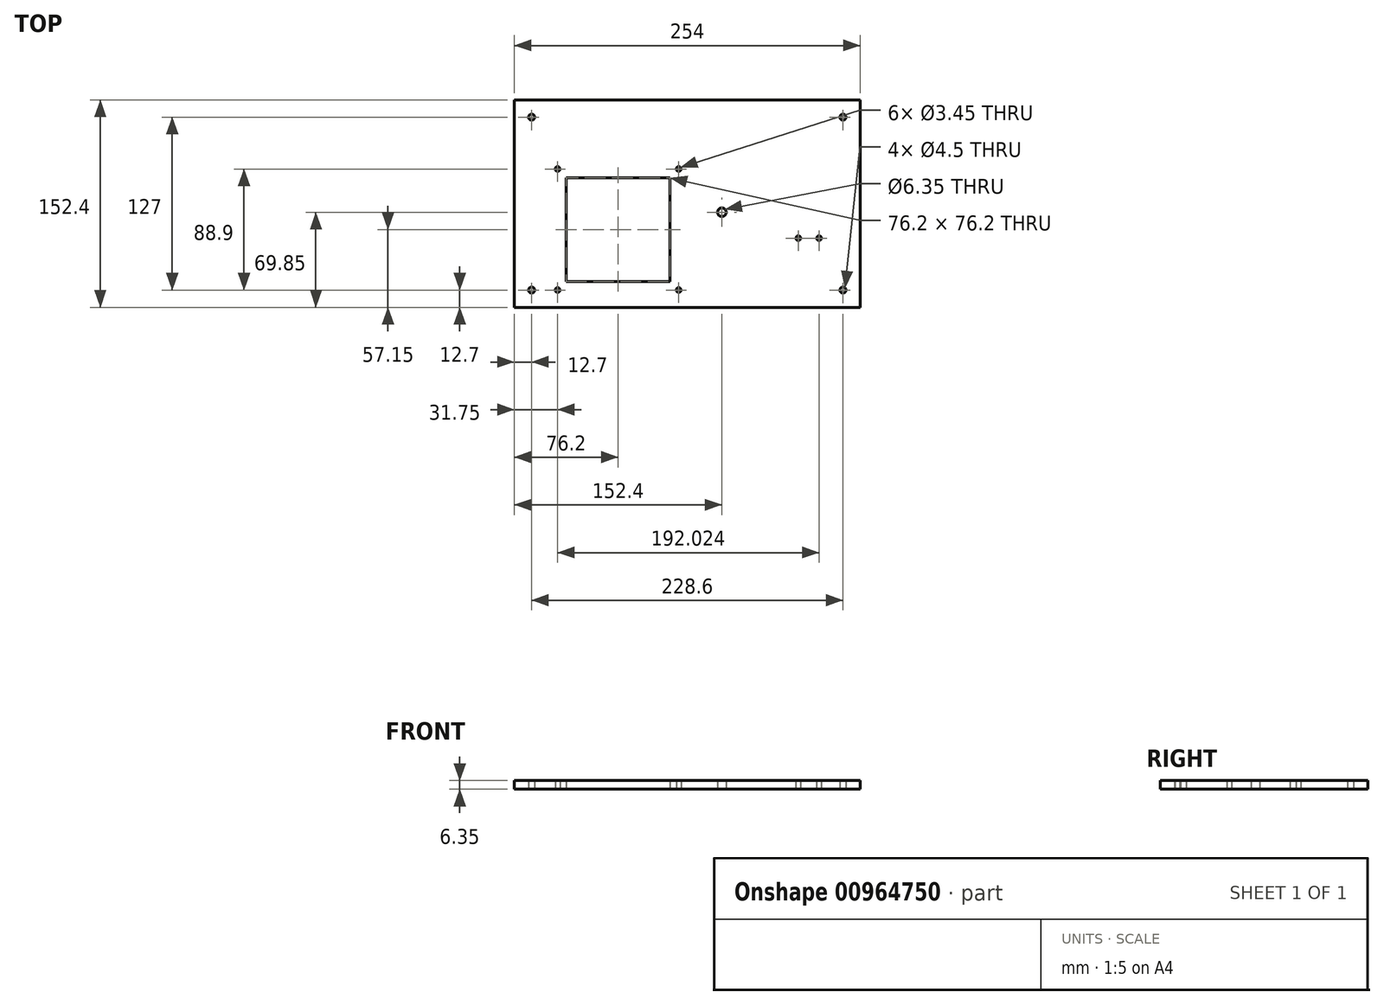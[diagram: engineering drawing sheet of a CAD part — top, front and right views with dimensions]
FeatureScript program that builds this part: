
annotation { "Feature Type Name" : "Feature", "Feature Type Description" : "" }
export const myFeature = defineFeature(function(context is Context, id is Id, definition is map)
    precondition{}
    {
        {
            var Q0;
            Q0=qCreatedBy(makeId("Top.planeOp"),FACE);
            var sketch = newSketch(context, id + "F0", { "sketchPlane" : qUnion([Q0])});
            skLineSegment(sketch, "E0.bottom", {"start": v(127, 76.2) * mm, "end": v(-127, 76.2) * mm});
            skLineSegment(sketch, "E0.top", {"start": v(127, -76.2) * mm, "end": v(-127, -76.2) * mm});
            skLineSegment(sketch, "E0.left", {"start": v(127, 76.2) * mm, "end": v(127, -76.2) * mm});
            skLineSegment(sketch, "E0.right", {"start": v(-127, 76.2) * mm, "end": v(-127, -76.2) * mm});
            skPoint(sketch, "E0.middle", {"position": v(0, 0) * mm});
            skLineSegment(sketch, "E1.bottom", {"start": v(-6.35, -63.5) * mm, "end": v(-95.25, -63.5) * mm, "construction": true});
            skLineSegment(sketch, "E1.top", {"start": v(-6.35, 25.4) * mm, "end": v(-95.25, 25.4) * mm, "construction": true});
            skLineSegment(sketch, "E1.left", {"start": v(-6.35, -63.5) * mm, "end": v(-6.35, 25.4) * mm, "construction": true});
            skLineSegment(sketch, "E1.right", {"start": v(-95.25, -63.5) * mm, "end": v(-95.25, 25.4) * mm, "construction": true});
            skPoint(sketch, "E1.middle", {"position": v(-50.8, -19.05) * mm});
            skCircle(sketch, "E2", {"center": v(-95.25, 25.4) * mm, "radius": 1.73 * mm});
            skCircle(sketch, "E3", {"center": v(-6.35, 25.4) * mm, "radius": 1.73 * mm});
            skCircle(sketch, "E4", {"center": v(-6.35, -63.5) * mm, "radius": 1.73 * mm});
            skCircle(sketch, "E5", {"center": v(-95.25, -63.5) * mm, "radius": 1.73 * mm});
            skLineSegment(sketch, "E6.bottom", {"start": v(-12.7, 19.05) * mm, "end": v(-88.9, 19.05) * mm});
            skLineSegment(sketch, "E6.top", {"start": v(-12.7, -57.15) * mm, "end": v(-88.9, -57.15) * mm});
            skLineSegment(sketch, "E6.left", {"start": v(-12.7, 19.05) * mm, "end": v(-12.7, -57.15) * mm});
            skLineSegment(sketch, "E6.right", {"start": v(-88.9, 19.05) * mm, "end": v(-88.9, -57.15) * mm});
            skLineSegment(sketch, "E7.bottom", {"start": v(114.3, 63.5) * mm, "end": v(-114.3, 63.5) * mm, "construction": true});
            skLineSegment(sketch, "E7.top", {"start": v(114.3, -63.5) * mm, "end": v(-114.3, -63.5) * mm, "construction": true});
            skLineSegment(sketch, "E7.left", {"start": v(114.3, 63.5) * mm, "end": v(114.3, -63.5) * mm, "construction": true});
            skLineSegment(sketch, "E7.right", {"start": v(-114.3, 63.5) * mm, "end": v(-114.3, -63.5) * mm, "construction": true});
            skCircle(sketch, "E8", {"center": v(-114.3, 63.5) * mm, "radius": 2.25 * mm});
            skCircle(sketch, "E9", {"center": v(-114.3, -63.5) * mm, "radius": 2.25 * mm});
            skCircle(sketch, "E10", {"center": v(114.3, 63.5) * mm, "radius": 2.25 * mm});
            skCircle(sketch, "E11", {"center": v(114.3, -63.5) * mm, "radius": 2.25 * mm});
            skLineSegment(sketch, "E12", {"start": v(-50.8, -6.35) * mm, "end": v(101.6, -6.35) * mm, "construction": true});
            skPoint(sketch, "E13", {"position": v(25.4, -6.35) * mm});
            skCircle(sketch, "E14", {"center": v(25.4, -6.35) * mm, "radius": 3.18 * mm});
            skCircle(sketch, "E15", {"center": v(81.53, -25.4) * mm, "radius": 1.73 * mm});
            skCircle(sketch, "E16", {"center": v(96.77, -25.4) * mm, "radius": 1.73 * mm});
            skSolve(sketch);
        }
        {
            var Q0;
            Q0 = qSketchRegion(id + "F0", true);
            extrude(context, id + "F1", {"entities" : qUnion([Q0]), "depth" : 6.35 * mm, "offsetDistance" : 25.4 * mm});
        }
    });
